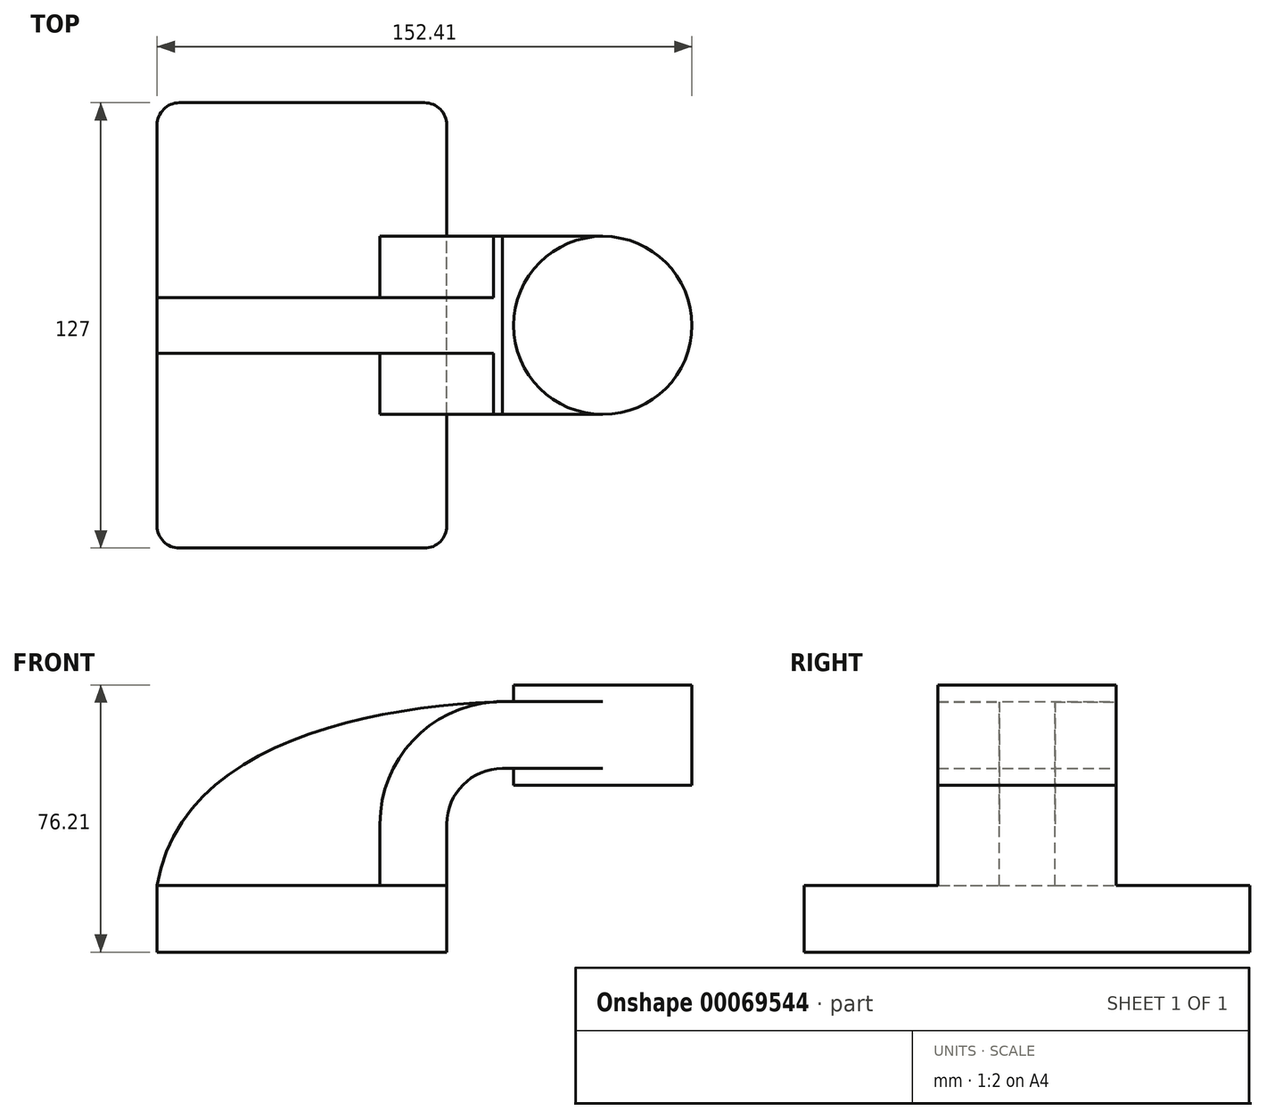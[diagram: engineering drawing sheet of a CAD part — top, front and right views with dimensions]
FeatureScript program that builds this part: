
annotation { "Feature Type Name" : "Feature", "Feature Type Description" : "" }
export const myFeature = defineFeature(function(context is Context, id is Id, definition is map)
    precondition{}
    {
        {
            var Q0;
            Q0=qCreatedBy(makeId("Front.planeOp"),FACE);
            var sketch = newSketch(context, id + "F0", { "sketchPlane" : qUnion([Q0])});
            skLineSegment(sketch, "E0.rect.bottom", {"start": v(-41.28, 9.53) * mm, "end": v(41.28, 9.53) * mm});
            skLineSegment(sketch, "E0.rect.top", {"start": v(-41.27, -9.53) * mm, "end": v(41.27, -9.53) * mm});
            skLineSegment(sketch, "E0.rect.left", {"start": v(-41.28, 9.53) * mm, "end": v(-41.28, -9.53) * mm});
            skLineSegment(sketch, "E0.rect.right", {"start": v(41.28, 9.53) * mm, "end": v(41.28, -9.53) * mm});
            skPoint(sketch, "E0.rect.middle", {"position": v(0, 0) * mm});
            skLineSegment(sketch, "E1", {"start": v(41.28, 9.53) * mm, "end": v(41.28, 26.99) * mm});
            skArc(sketch, "E2", {"start": v(57.15, 42.86) * mm, "mid": v(45.92, 38.21) * mm, "end": v(41.28, 26.99) * mm});
            skLineSegment(sketch, "E3.rect.bottom", {"start": v(111.12, 38.1) * mm, "end": v(60.32, 38.1) * mm});
            skLineSegment(sketch, "E3.rect.top", {"start": v(111.12, 66.67) * mm, "end": v(60.32, 66.67) * mm});
            skLineSegment(sketch, "E3.rect.left", {"start": v(111.12, 38.1) * mm, "end": v(111.12, 66.67) * mm});
            skLineSegment(sketch, "E3.rect.right", {"start": v(60.32, 38.1) * mm, "end": v(60.32, 66.67) * mm});
            skPoint(sketch, "E3.rect.middle", {"position": v(85.73, 52.39) * mm});
            skLineSegment(sketch, "E4", {"start": v(85.72, 66.67) * mm, "end": v(85.72, 38.1) * mm});
            skLineSegment(sketch, "E5", {"start": v(85.72, 42.86) * mm, "end": v(57.15, 42.86) * mm});
            skLineSegment(sketch, "E6.0", {"start": v(22.22, 9.53) * mm, "end": v(22.22, 26.99) * mm});
            skArc(sketch, "E6.1", {"start": v(57.15, 61.91) * mm, "mid": v(32.45, 51.68) * mm, "end": v(22.23, 26.99) * mm});
            skLineSegment(sketch, "E6.2", {"start": v(85.72, 61.91) * mm, "end": v(57.15, 61.91) * mm});
            skFitSpline(sketch, "E7", {"points": [v(-41.27, 9.52) * mm, v(57.15, 61.91) * mm], "startDerivative": vector(19.23, 120.21) * mm, "endDerivative": vector(115.46, 3.61) * mm});
            skSolve(sketch);
        }
        {
            var Q0;
            Q0=makeQuery(id+"F0.imprint","IMPRINT",FACE,{"disambiguationData":[TD([[makeQuery(id+"F0.imprint","IMPRINT",EDGE,{"derivedFrom":sQuery(id+"F0.wireOp",EDGE,"E0.rect.top")}),1.0]])]});
            extrude(context, id + "F1", {"entities" : qUnion([Q0]), "endBound" : BoundingType.SYMMETRIC, "depth" : 127 * mm});
        }
        {
            var Q0;
            {var subQ9=sQuery(id+"F0.wireOp",EDGE,"E1");Q0=makeQuery(id+"F0.imprint","IMPRINT",FACE,{"disambiguationData":[TD([[makeQuery(id+"F0.imprint","IMPRINT",EDGE,{"derivedFrom":subQ9}),1.0]])]});}
            var Q1;
            {var subQ0=sQuery(id+"F0.wireOp",EDGE,"E5");var subQ1=sQuery(id+"F0.wireOp",EDGE,"E3.rect.right");var subQ2=makeQuery(id+"F0.imprint","INTERSECT",VERTEX,{"derivedFrom":[subQ1,subQ0]});Q1=makeQuery(id+"F0.imprint","IMPRINT",FACE,{"disambiguationData":[TD([[makeQuery(id+"F0.imprint","IMPRINT",EDGE,{"disambiguationData":[TD([[subQ2,-1.0]])],"derivedFrom":subQ1}),-1.0]])]});}
            extrude(context, id + "F2", {"entities" : qUnion([Q0, Q1]), "operationType" : NewBodyOperationType.ADD, "endBound" : BoundingType.SYMMETRIC, "depth" : 50.8 * mm});
        }
        {
            var Q0;
            {var subQ3=sQuery(id+"F0.wireOp",EDGE,"E6.0");Q0=makeQuery(id+"F0.imprint","IMPRINT",FACE,{"disambiguationData":[TD([[makeQuery(id+"F0.imprint","IMPRINT",EDGE,{"derivedFrom":subQ3}),1.0]])]});}
            extrude(context, id + "F3", {"entities" : qUnion([Q0]), "operationType" : NewBodyOperationType.ADD, "endBound" : BoundingType.SYMMETRIC, "depth" : 15.88 * mm});
        }
        {
            var Q0;
            {var subQ4=sQuery(id+"F0.wireOp",EDGE,"E3.rect.left");Q0=makeQuery(id+"F0.imprint","IMPRINT",FACE,{"disambiguationData":[TD([[makeQuery(id+"F0.imprint","IMPRINT",EDGE,{"derivedFrom":subQ4}),1.0]])]});}
            var Q1;
            Q1=sQuery(id+"F0.wireOp",EDGE,"E4");
            revolve(context, id + "F4", {"operationType" : NewBodyOperationType.ADD, "entities" : qUnion([Q0]), "axis" : qUnion([Q1]), "revolveType" : RevolveType.FULL});
        }
        {
            var Q0;
            Q0=makeQuery(id+"F1.opExtrude","CAP_EDGE",EDGE,{"disambiguationData":[OSD([sQuery(id+"F0.wireOp",EDGE,"E0.rect.right")])],"isStart":false});
            var Q1;
            Q1=makeQuery(id+"F1.opExtrude","CAP_EDGE",EDGE,{"disambiguationData":[OSD([sQuery(id+"F0.wireOp",EDGE,"E0.rect.left")])],"isStart":false});
            var Q2;
            Q2=makeQuery(id+"F1.opExtrude","CAP_EDGE",EDGE,{"disambiguationData":[OSD([sQuery(id+"F0.wireOp",EDGE,"E0.rect.right")])],"isStart":true});
            var Q3;
            Q3=makeQuery(id+"F1.opExtrude","CAP_EDGE",EDGE,{"disambiguationData":[OSD([sQuery(id+"F0.wireOp",EDGE,"E0.rect.left")])],"isStart":true});
            fillet(context, id + "F5", {"entities" : qUnion([Q0, Q1, Q2, Q3]), "radius" : 6.35 * mm, "tangentPropagation" : true, "allowEdgeOverflow" : false});
        }
    });
